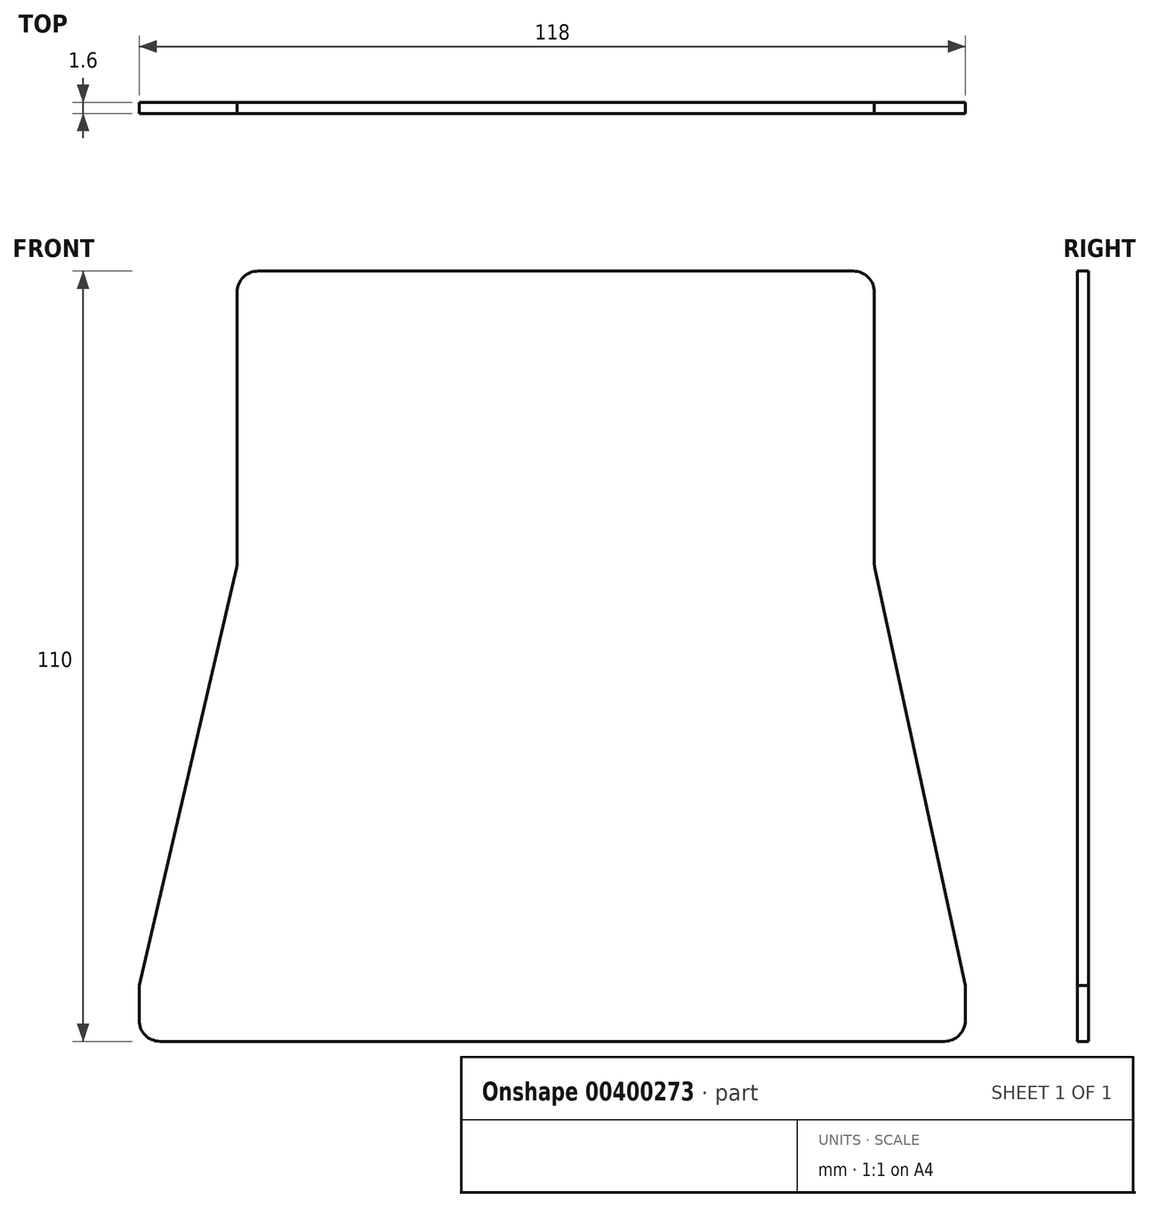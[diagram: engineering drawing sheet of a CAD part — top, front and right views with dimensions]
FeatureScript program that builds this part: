
annotation { "Feature Type Name" : "Feature", "Feature Type Description" : "" }
export const myFeature = defineFeature(function(context is Context, id is Id, definition is map)
    precondition{}
    {
        {
            var Q0;
            Q0=qCreatedBy(makeId("Front.planeOp"),FACE);
            var sketch = newSketch(context, id + "F0", { "sketchPlane" : qUnion([Q0])});
            skLineSegment(sketch, "E0.top", {"start": v(58.5, -68) * mm, "end": v(-59.5, -68) * mm});
            skLineSegment(sketch, "E1", {"start": v(45.5, 0) * mm, "end": v(45.5, 42) * mm});
            skLineSegment(sketch, "E2", {"start": v(45.5, 42) * mm, "end": v(-45.5, 42) * mm});
            skLineSegment(sketch, "E3", {"start": v(-45.5, 0) * mm, "end": v(-45.5, 42) * mm});
            skLineSegment(sketch, "E4", {"start": v(58.5, -68) * mm, "end": v(58.5, -60) * mm});
            skLineSegment(sketch, "E5", {"start": v(-59.5, -68) * mm, "end": v(-59.5, -60) * mm});
            skLineSegment(sketch, "E6", {"start": v(45.5, 0) * mm, "end": v(58.5, -60) * mm});
            skLineSegment(sketch, "E7", {"start": v(-45.5, 0) * mm, "end": v(-59.5, -60) * mm});
            skSolve(sketch);
        }
        {
            var Q0;
            Q0=makeQuery(id+"F0.imprint","IMPRINT",FACE,{"disambiguationData":[TD([[makeQuery(id+"F0.imprint","IMPRINT",EDGE,{"derivedFrom":sQuery(id+"F0.wireOp",EDGE,"E0.top")}),-1.0]])]});
            extrude(context, id + "F1", {"entities" : qUnion([Q0]), "depth" : 1.6 * mm, "offsetDistance" : 25 * mm});
        }
        {
            var Q0;
            Q0=makeQuery(id+"F1.opExtrude","SWEPT_EDGE",EDGE,{"disambiguationData":[OSD([sQuery(id+"F0.wireOp",EDGE,"E0.top"),sQuery(id+"F0.wireOp",EDGE,"E5")])]});
            var Q1;
            Q1=makeQuery(id+"F1.opExtrude","SWEPT_EDGE",EDGE,{"disambiguationData":[OSD([sQuery(id+"F0.wireOp",EDGE,"E0.top"),sQuery(id+"F0.wireOp",EDGE,"E4")])]});
            var Q2;
            Q2=makeQuery(id+"F1.opExtrude","SWEPT_EDGE",EDGE,{"disambiguationData":[OSD([sQuery(id+"F0.wireOp",EDGE,"E2"),sQuery(id+"F0.wireOp",EDGE,"E3")])]});
            var Q3;
            Q3=makeQuery(id+"F1.opExtrude","SWEPT_EDGE",EDGE,{"disambiguationData":[OSD([sQuery(id+"F0.wireOp",EDGE,"E1"),sQuery(id+"F0.wireOp",EDGE,"E2")])]});
            var Q4;
            Q4=makeQuery(id+"F1.opExtrude","SWEPT_EDGE",EDGE,{"disambiguationData":[OSD([sQuery(id+"F0.wireOp",EDGE,"E1"),sQuery(id+"F0.wireOp",EDGE,"E6")])]});
            var Q5;
            Q5=makeQuery(id+"F1.opExtrude","SWEPT_EDGE",EDGE,{"disambiguationData":[OSD([sQuery(id+"F0.wireOp",EDGE,"E3"),sQuery(id+"F0.wireOp",EDGE,"E7")])]});
            fillet(context, id + "F2", {"entities" : qUnion([Q0, Q1, Q2, Q3, Q4, Q5]), "radius" : 3 * mm, "tangentPropagation" : true, "allowEdgeOverflow" : false});
        }
    });
